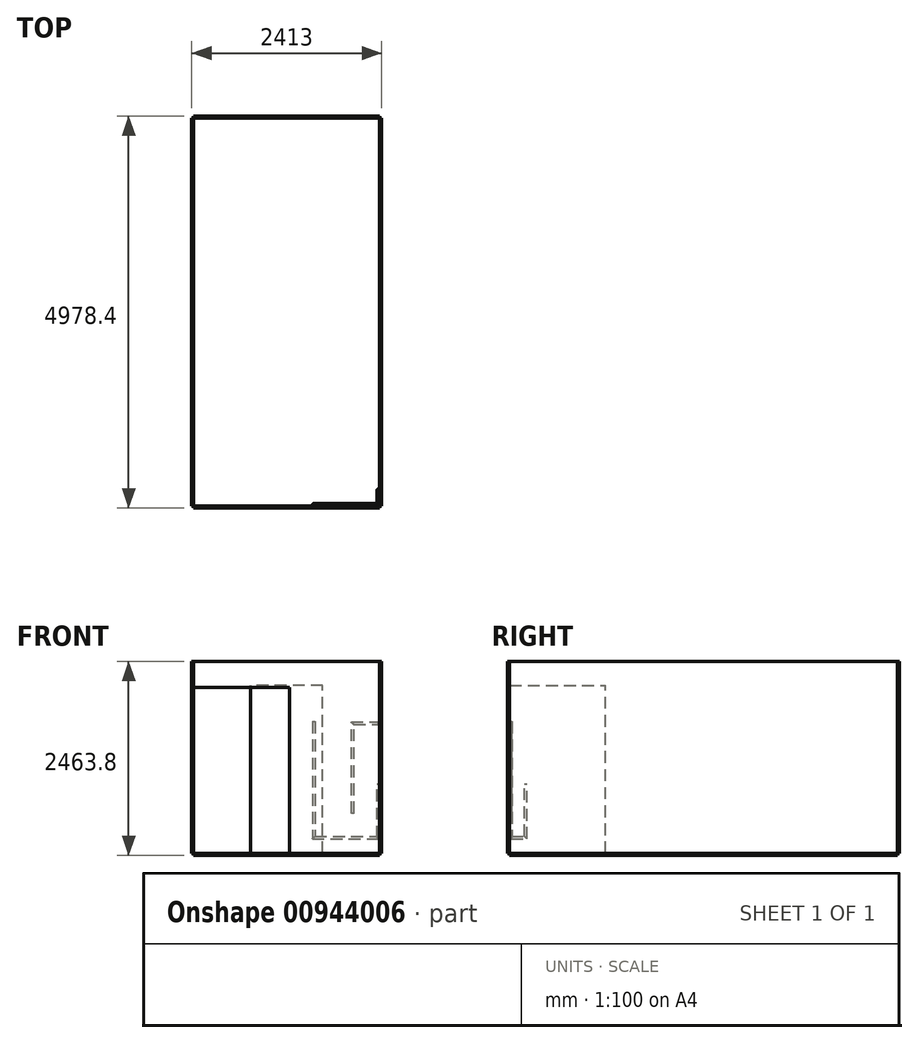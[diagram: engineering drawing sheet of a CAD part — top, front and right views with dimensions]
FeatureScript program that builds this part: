
annotation { "Feature Type Name" : "Feature", "Feature Type Description" : "" }
export const myFeature = defineFeature(function(context is Context, id is Id, definition is map)
    precondition{}
    {
        {
            var Q0;
            Q0=qCreatedBy(makeId("Top.planeOp"),FACE);
            var sketch = newSketch(context, id + "F0", { "sketchPlane" : qUnion([Q0])});
            skLineSegment(sketch, "E0.bottom", {"start": v(0, 0) * mm, "end": v(2362.2, 0) * mm});
            skLineSegment(sketch, "E0.top", {"start": v(0, 4927.6) * mm, "end": v(2362.2, 4927.6) * mm});
            skLineSegment(sketch, "E0.left", {"start": v(0, 0) * mm, "end": v(0, 4927.6) * mm});
            skLineSegment(sketch, "E0.right", {"start": v(2362.2, 0) * mm, "end": v(2362.2, 4927.6) * mm});
            skSolve(sketch);
        }
        {
            var Q0;
            Q0 = qSketchRegion(id + "F0", true);
            extrude(context, id + "F1", {"entities" : qUnion([Q0]), "depth" : 25.4 * mm, "offsetDistance" : 25.4 * mm});
        }
        {
            var Q0;
            Q0=makeQuery(id+"F1.opExtrude","CAP_FACE",FACE,{"disambiguationData":[OSD([sQuery(id+"F0.wireOp",EDGE,"E0.bottom"),sQuery(id+"F0.wireOp",EDGE,"E0.top"),sQuery(id+"F0.wireOp",EDGE,"E0.left"),sQuery(id+"F0.wireOp",EDGE,"E0.right")])],"isStart":false});
            var sketch = newSketch(context, id + "F2", { "sketchPlane" : qUnion([Q0])});
            skLineSegment(sketch, "E1.bottom", {"start": v(0, 4927.6) * mm, "end": v(-25.4, 4927.6) * mm});
            skLineSegment(sketch, "E1.top", {"start": v(0, 0) * mm, "end": v(-25.4, 0) * mm});
            skLineSegment(sketch, "E1.left", {"start": v(0, 4927.6) * mm, "end": v(0, 0) * mm});
            skLineSegment(sketch, "E1.right", {"start": v(-25.4, 4927.6) * mm, "end": v(-25.4, 0) * mm});
            skLineSegment(sketch, "E2.bottom", {"start": v(2362.2, 4927.6) * mm, "end": v(2387.6, 4927.6) * mm});
            skLineSegment(sketch, "E2.top", {"start": v(2362.2, 0) * mm, "end": v(2387.6, 0) * mm});
            skLineSegment(sketch, "E2.left", {"start": v(2362.2, 4927.6) * mm, "end": v(2362.2, 0) * mm});
            skLineSegment(sketch, "E2.right", {"start": v(2387.6, 4927.6) * mm, "end": v(2387.6, 0) * mm});
            skSolve(sketch);
        }
        {
            var Q0;
            Q0 = qSketchRegion(id + "F2", true);
            extrude(context, id + "F3", {"entities" : qUnion([Q0]), "depth" : 2438.4 * mm, "offsetDistance" : 25.4 * mm});
        }
        {
            var Q0;
            Q0=makeQuery(id+"F1.opExtrude","CAP_FACE",FACE,{"disambiguationData":[OSD([sQuery(id+"F0.wireOp",EDGE,"E0.bottom"),sQuery(id+"F0.wireOp",EDGE,"E0.top"),sQuery(id+"F0.wireOp",EDGE,"E0.left"),sQuery(id+"F0.wireOp",EDGE,"E0.right")])],"isStart":false});
            var sketch = newSketch(context, id + "F4", { "sketchPlane" : qUnion([Q0])});
            skLineSegment(sketch, "E3.bottom", {"start": v(0, 4927.6) * mm, "end": v(2362.2, 4927.6) * mm});
            skLineSegment(sketch, "E3.top", {"start": v(0, 4953) * mm, "end": v(2362.2, 4953) * mm});
            skLineSegment(sketch, "E3.left", {"start": v(0, 4927.6) * mm, "end": v(0, 4953) * mm});
            skLineSegment(sketch, "E3.right", {"start": v(2362.2, 4927.6) * mm, "end": v(2362.2, 4953) * mm});
            skLineSegment(sketch, "E4.bottom", {"start": v(0, 0) * mm, "end": v(2362.2, 0) * mm});
            skLineSegment(sketch, "E4.top", {"start": v(0, -25.4) * mm, "end": v(2362.2, -25.4) * mm});
            skLineSegment(sketch, "E4.left", {"start": v(0, 0) * mm, "end": v(0, -25.4) * mm});
            skLineSegment(sketch, "E4.right", {"start": v(2362.2, 0) * mm, "end": v(2362.2, -25.4) * mm});
            skSolve(sketch);
        }
        {
            var Q0;
            Q0 = qSketchRegion(id + "F4", true);
            extrude(context, id + "F5", {"entities" : qUnion([Q0]), "depth" : 2438.4 * mm, "offsetDistance" : 25.4 * mm});
        }
        {
            var Q0;
            Q0=makeQuery(id+"F5.opExtrude","SWEPT_FACE",FACE,{"disambiguationData":[OSD([sQuery(id+"F4.wireOp",EDGE,"E3.bottom")])]});
            var sketch = newSketch(context, id + "F6", { "sketchPlane" : qUnion([Q0])});
            skLineSegment(sketch, "E5.bottom", {"start": v(1638.3, 25.4) * mm, "end": v(723.9, 25.4) * mm});
            skLineSegment(sketch, "E5.top", {"start": v(1638.3, 2159) * mm, "end": v(723.9, 2159) * mm});
            skLineSegment(sketch, "E5.left", {"start": v(1638.3, 25.4) * mm, "end": v(1638.3, 2159) * mm});
            skLineSegment(sketch, "E5.right", {"start": v(723.9, 25.4) * mm, "end": v(723.9, 2159) * mm});
            skPoint(sketch, "E6", {"position": v(1181.1, 25.4) * mm});
            skSolve(sketch);
        }
        {
            var Q0;
            Q0 = qSketchRegion(id + "F6", true);
            extrude(context, id + "F7", {"entities" : qUnion([Q0]), "operationType" : NewBodyOperationType.REMOVE, "endBound" : BoundingType.THROUGH_ALL, "oppositeDirection" : true, "depth" : 25.4 * mm, "offsetDistance" : 25.4 * mm});
        }
        {
            var Q0;
            Q0=makeQuery(id+"F3.opExtrude","SWEPT_FACE",FACE,{"disambiguationData":[OSD([sQuery(id+"F2.wireOp",EDGE,"E1.left")])]});
            var sketch = newSketch(context, id + "F8", { "sketchPlane" : qUnion([Q0])});
            skLineSegment(sketch, "E7.bottom", {"start": v(0, 25.4) * mm, "end": v(1219.2, 25.4) * mm});
            skLineSegment(sketch, "E7.top", {"start": v(0, 2159) * mm, "end": v(1219.2, 2159) * mm});
            skLineSegment(sketch, "E7.left", {"start": v(0, 25.4) * mm, "end": v(0, 2159) * mm});
            skLineSegment(sketch, "E7.right", {"start": v(1219.2, 25.4) * mm, "end": v(1219.2, 2159) * mm});
            skSolve(sketch);
        }
        {
            var Q0;
            Q0 = qSketchRegion(id + "F8", true);
            extrude(context, id + "F9", {"entities" : qUnion([Q0]), "operationType" : NewBodyOperationType.REMOVE, "endBound" : BoundingType.THROUGH_ALL, "oppositeDirection" : true, "depth" : 25.4 * mm, "offsetDistance" : 25.4 * mm});
        }
        {
            var Q0;
            Q0=makeQuery(id+"F5.opExtrude","SWEPT_FACE",FACE,{"disambiguationData":[OSD([sQuery(id+"F4.wireOp",EDGE,"E4.bottom")])]});
            var sketch = newSketch(context, id + "F10", { "sketchPlane" : qUnion([Q0])});
            skLineSegment(sketch, "E8.bottom", {"start": v(0, 0) * mm, "end": v(-1219.2, 0) * mm});
            skLineSegment(sketch, "E8.top", {"start": v(0, 2133.6) * mm, "end": v(-1219.2, 2133.6) * mm});
            skLineSegment(sketch, "E8.left", {"start": v(0, 0) * mm, "end": v(0, 2133.6) * mm});
            skLineSegment(sketch, "E8.right", {"start": v(-1219.2, 0) * mm, "end": v(-1219.2, 2133.6) * mm});
            skSolve(sketch);
        }
        {
            var Q0;
            Q0 = qSketchRegion(id + "F10", true);
            extrude(context, id + "F11", {"entities" : qUnion([Q0]), "operationType" : NewBodyOperationType.REMOVE, "oppositeDirection" : true, "depth" : 25.4 * mm, "offsetDistance" : 25.4 * mm});
        }
        {
            var Q0;
            Q0=makeQuery(id+"F1.opExtrude","CAP_FACE",FACE,{"disambiguationData":[OSD([sQuery(id+"F0.wireOp",EDGE,"E0.bottom"),sQuery(id+"F0.wireOp",EDGE,"E0.top"),sQuery(id+"F0.wireOp",EDGE,"E0.left"),sQuery(id+"F0.wireOp",EDGE,"E0.right")])],"isStart":false});
            cPlane(context, id + "F12", {"entities" : qUnion([Q0]), "cplaneType" : CPlaneType.OFFSET, "offset" : 1676.4 * mm, "width" : 152.4 * mm, "height" : 152.4 * mm});
        }
        {
            var Q0;
            Q0=makeQuery(id+"F5.opExtrude","SWEPT_FACE",FACE,{"disambiguationData":[OSD([sQuery(id+"F4.wireOp",EDGE,"E4.bottom")])]});
            cPlane(context, id + "F13", {"entities" : qUnion([Q0]), "cplaneType" : CPlaneType.OFFSET, "offset" : 15.88 * mm, "width" : 152.4 * mm, "height" : 152.4 * mm});
        }
        {
            var Q0;
            Q0=makeQuery(id+"F3.opExtrude","SWEPT_FACE",FACE,{"disambiguationData":[OSD([sQuery(id+"F2.wireOp",EDGE,"E2.left")])]});
            cPlane(context, id + "F14", {"entities" : qUnion([Q0]), "cplaneType" : CPlaneType.OFFSET, "offset" : 15.88 * mm, "width" : 152.4 * mm, "height" : 152.4 * mm});
        }
        {
            var Q0;
            Q0=makeQuery(id+"F1.opExtrude","CAP_FACE",FACE,{"disambiguationData":[OSD([sQuery(id+"F0.wireOp",EDGE,"E0.bottom"),sQuery(id+"F0.wireOp",EDGE,"E0.top"),sQuery(id+"F0.wireOp",EDGE,"E0.left"),sQuery(id+"F0.wireOp",EDGE,"E0.right")])],"isStart":false});
            cPlane(context, id + "F15", {"entities" : qUnion([Q0]), "cplaneType" : CPlaneType.OFFSET, "offset" : 508 * mm, "width" : 152.4 * mm, "height" : 152.4 * mm});
        }
        {
            var Q0;
            Q0=qCreatedBy(id+"F14.planeOp",FACE);
            var sketch = newSketch(context, id + "F16", { "sketchPlane" : qUnion([Q0])});
            skLineSegment(sketch, "E9", {"start": v(-203.18, 226.9) * mm, "end": v(-203.18, 904.3) * mm});
            skLineSegment(sketch, "E10", {"start": v(-203.18, 226.9) * mm, "end": v(-15.87, 226.9) * mm});
            skSolve(sketch);
        }
        {
            var Q0;
            Q0=qCreatedBy(id+"F13.planeOp",FACE);
            var sketch = newSketch(context, id + "F17", { "sketchPlane" : qUnion([Q0])});
            skLineSegment(sketch, "E11", {"start": v(-1523.06, 1701.8) * mm, "end": v(-1523.06, 226.9) * mm});
            skLineSegment(sketch, "E12", {"start": v(-1523.06, 226.9) * mm, "end": v(-2346.33, 226.9) * mm});
            skSolve(sketch);
        }
        {
            var Q0;
            Q0=qCreatedBy(id+"F12.planeOp",FACE);
            var sketch = newSketch(context, id + "F18", { "sketchPlane" : qUnion([Q0])});
            skCircle(sketch, "E13", {"center": v(1523, 15.88) * mm, "radius": 15.88 * mm});
            skPoint(sketch, "E13.first.point", {"position": v(1523, 0) * mm});
            skPoint(sketch, "E13.second.point", {"position": v(1513.66, 3.03) * mm});
            skPoint(sketch, "E13.third.point", {"position": v(1535.54, 25.6) * mm});
            skSolve(sketch);
        }
        {
            var Q0;
            Q0 = qSketchRegion(id + "F18", true);
            var Q1;
            Q1 = qConstructionFilter(qBodyType(qCreatedBy(id + "F17" ,EDGE), BodyType.WIRE), ConstructionObject.NO);
            var Q2;
            Q2 = qConstructionFilter(qBodyType(qCreatedBy(id + "F16" ,EDGE), BodyType.WIRE), ConstructionObject.NO);
            sweep(context, id + "F19", {"profiles" : qUnion([Q0]), "path" : qUnion([Q1, Q2])});
        }
        {
            var Q0;
            Q0=qCreatedBy(id+"F15.planeOp",FACE);
            var sketch = newSketch(context, id + "F20", { "sketchPlane" : qUnion([Q0])});
            skCircle(sketch, "E14", {"center": v(2016.95, 15.88) * mm, "radius": 15.88 * mm});
            skSolve(sketch);
        }
        {
            var Q0;
            Q0=qCreatedBy(id+"F13.planeOp",FACE);
            var sketch = newSketch(context, id + "F21", { "sketchPlane" : qUnion([Q0])});
            skLineSegment(sketch, "E15", {"start": v(-2016.95, 533.4) * mm, "end": v(-2016.95, 1680.67) * mm});
            skLineSegment(sketch, "E16", {"start": v(-2016.95, 1680.67) * mm, "end": v(-2346.33, 1680.67) * mm});
            skSolve(sketch);
        }
        {
            var Q0;
            Q0 = qSketchRegion(id + "F20", true);
            var Q1;
            Q1 = qConstructionFilter(qBodyType(qCreatedBy(id + "F21" ,EDGE), BodyType.WIRE), ConstructionObject.NO);
            var Q2;
            Q2 = qConstructionFilter(qBodyType(qCreatedBy(id + "FegF0oFswAq2Nqb_6" ,EDGE), BodyType.WIRE), ConstructionObject.NO);
            sweep(context, id + "F22", {"profiles" : qUnion([Q0]), "path" : qUnion([Q1, Q2])});
        }
    });
